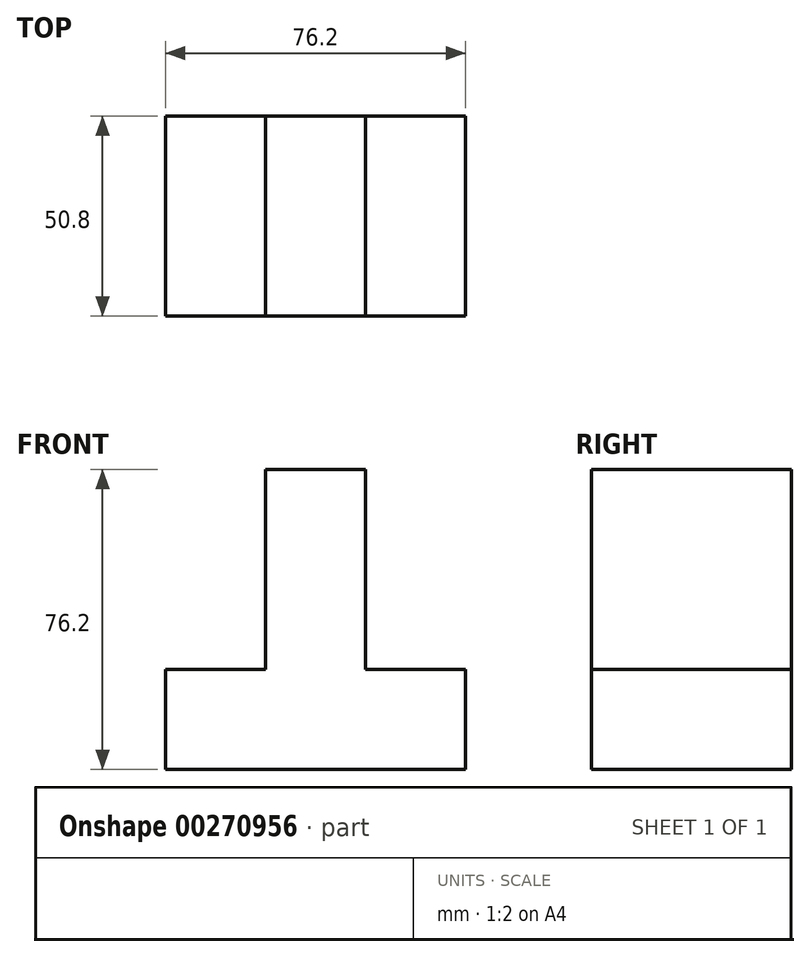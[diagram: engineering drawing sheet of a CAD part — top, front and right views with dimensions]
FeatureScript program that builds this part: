
annotation { "Feature Type Name" : "Feature", "Feature Type Description" : "" }
export const myFeature = defineFeature(function(context is Context, id is Id, definition is map)
    precondition{}
    {
        {
            var Q0;
            Q0=qCreatedBy(makeId("Front.planeOp"),FACE);
            var sketch = newSketch(context, id + "F0", { "sketchPlane" : qUnion([Q0])});
            skLineSegment(sketch, "E0", {"start": v(-50.8, 0) * mm, "end": v(0, 0) * mm});
            skLineSegment(sketch, "E1", {"start": v(-50.8, 0) * mm, "end": v(-50.8, 25.4) * mm});
            skLineSegment(sketch, "E2", {"start": v(-50.8, 25.4) * mm, "end": v(-25.4, 25.4) * mm});
            skLineSegment(sketch, "E3", {"start": v(-25.4, 25.4) * mm, "end": v(-25.4, 76.2) * mm});
            skLineSegment(sketch, "E4", {"start": v(-25.4, 76.2) * mm, "end": v(0, 76.2) * mm});
            skLineSegment(sketch, "E5", {"start": v(0, 76.2) * mm, "end": v(0, 25.4) * mm});
            skLineSegment(sketch, "E6", {"start": v(0, 25.4) * mm, "end": v(25.4, 25.4) * mm});
            skLineSegment(sketch, "E7", {"start": v(25.4, 25.4) * mm, "end": v(25.4, 0) * mm});
            skLineSegment(sketch, "E8", {"start": v(25.4, 0) * mm, "end": v(0, 0) * mm});
            skSolve(sketch);
        }
        {
            var Q0;
            Q0 = qSketchRegion(id + "F0", true);
            extrude(context, id + "F1", {"entities" : qUnion([Q0]), "depth" : 50.8 * mm});
        }
    });
